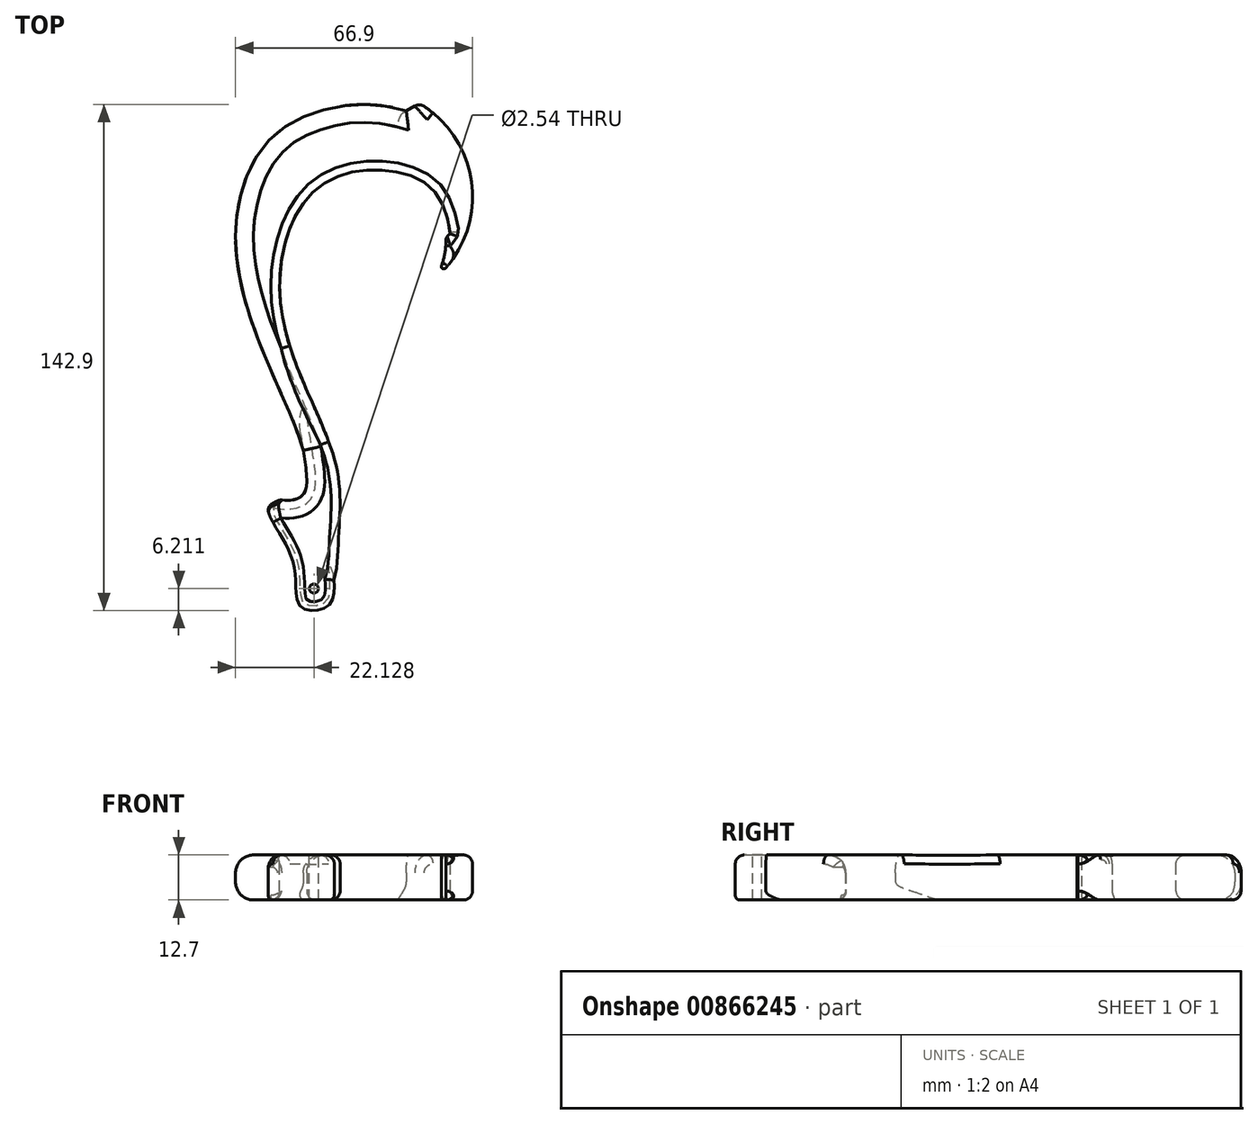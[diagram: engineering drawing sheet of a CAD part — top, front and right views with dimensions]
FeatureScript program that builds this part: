
annotation { "Feature Type Name" : "Feature", "Feature Type Description" : "" }
export const myFeature = defineFeature(function(context is Context, id is Id, definition is map)
    precondition{}
    {
        {
            var Q0;
            Q0=qCreatedBy(makeId("Top.planeOp"),FACE);
            var sketch = newSketch(context, id + "F0", { "sketchPlane" : qUnion([Q0])});
            skFitSpline(sketch, "E0", {"points": [v(12.36, 30.58) * mm, v(0, 47.37) * mm, v(-24.9, 43.6) * mm, v(-35.15, 8.04) * mm, v(-20.04, -34.04) * mm, v(-19.17, -55.17) * mm, v(-20.47, -67.18) * mm], "startDerivative": vector(-26.58, 212.62) * mm, "endDerivative": vector(-34.09, -129.53) * mm});
            skLineSegment(sketch, "E1", {"start": v(12.36, 30.58) * mm, "end": v(11.16, 29.44) * mm});
            skLineSegment(sketch, "E2", {"start": v(3.7, 67.39) * mm, "end": v(0, 65.26) * mm});
            skFitSpline(sketch, "E3", {"points": [v(0, 65.26) * mm, v(-24.38, 65.26) * mm, v(-40.44, 55.04) * mm, v(-48.04, 24.97) * mm, v(-35.77, -13.58) * mm, v(-29.1, -30.6) * mm], "startDerivative": vector(-144.73, 42.7) * mm, "endDerivative": vector(33.48, -115.11) * mm});
            skArc(sketch, "E4", {"start": v(11.16, 20.94) * mm, "mid": v(18.28, 45.9) * mm, "end": v(3.7, 67.39) * mm});
            skArc(sketch, "E5", {"start": v(10.08, 21.93) * mm, "mid": v(10.97, 25.63) * mm, "end": v(11.16, 29.44) * mm});
            skArc(sketch, "E6", {"start": v(10.08, 21.93) * mm, "mid": v(10.1, 20.86) * mm, "end": v(11.16, 20.94) * mm});
            skFitSpline(sketch, "E7", {"points": [v(-29.1, -30.6) * mm, v(-29.1, -42.96) * mm, v(-35.77, -44.53) * mm], "startDerivative": vector(5.3, -33.07) * mm, "endDerivative": vector(-21.74, 3.06) * mm});
            skFitSpline(sketch, "E8", {"points": [v(-35.77, -44.53) * mm, v(-38.98, -47.16) * mm, v(-31.97, -62.05) * mm, v(-29.81, -74.7) * mm, v(-22.03, -74.45) * mm, v(-20.47, -67.18) * mm], "startDerivative": vector(-32.87, -15.99) * mm, "endDerivative": vector(-3.2, 46.84) * mm});
            skSolve(sketch);
        }
        {
            var Q0;
            Q0=makeQuery(id+"F0.imprint","IMPRINT",FACE,{"disambiguationData":[TD([[makeQuery(id+"F0.imprint","IMPRINT",EDGE,{"derivedFrom":sQuery(id+"F0.wireOp",EDGE,"E0")}),-1.0]])]});
            extrude(context, id + "F1", {"entities" : qUnion([Q0]), "depth" : 12.7 * mm, "offsetDistance" : 25.4 * mm});
        }
        {
            var Q0;
            Q0=makeQuery(id+"F1.opExtrude","CAP_EDGE",EDGE,{"disambiguationData":[OSD([sQuery(id+"F0.wireOp",EDGE,"E3")])],"isStart":false});
            var Q1;
            Q1=makeQuery(id+"F1.opExtrude","CAP_EDGE",EDGE,{"disambiguationData":[OSD([sQuery(id+"F0.wireOp",EDGE,"E2")])],"isStart":false});
            var Q2;
            Q2=makeQuery(id+"F1.opExtrude","CAP_EDGE",EDGE,{"disambiguationData":[OSD([sQuery(id+"F0.wireOp",EDGE,"E7")])],"isStart":false});
            fillet(context, id + "F2", {"entities" : qUnion([Q0, Q1, Q2]), "radius" : 5.08 * mm, "tangentPropagation" : true, "allowEdgeOverflow" : false});
        }
        {
            var Q0;
            Q0=makeQuery(id+"F1.opExtrude","CAP_EDGE",EDGE,{"disambiguationData":[OSD([sQuery(id+"F0.wireOp",EDGE,"E0")])],"isStart":false});
            fillet(context, id + "F3", {"entities" : qUnion([Q0]), "radius" : 2.5 * mm, "tangentPropagation" : true, "allowEdgeOverflow" : false});
        }
        {
            var Q0;
            Q0=makeQuery(id+"F1.opExtrude","CAP_EDGE",EDGE,{"disambiguationData":[OSD([sQuery(id+"F0.wireOp",EDGE,"E8")])],"isStart":false});
            var Q1;
            Q1=makeQuery(id+"F1.opExtrude","CAP_EDGE",EDGE,{"disambiguationData":[OSD([sQuery(id+"F0.wireOp",EDGE,"E1")])],"isStart":false});
            fillet(context, id + "F4", {"entities" : qUnion([Q0, Q1]), "radius" : 2.5 * mm, "tangentPropagation" : true, "allowEdgeOverflow" : false});
        }
        {
            var Q0;
            Q0=makeQuery(id+"F1.opExtrude","CAP_EDGE",EDGE,{"disambiguationData":[OSD([sQuery(id+"F0.wireOp",EDGE,"E5")])],"isStart":false});
            fillet(context, id + "F5", {"entities" : qUnion([Q0]), "radius" : 1.27 * mm, "tangentPropagation" : true, "allowEdgeOverflow" : false});
        }
        {
            var Q0;
            Q0=makeQuery(id+"F1.opExtrude","CAP_EDGE",EDGE,{"disambiguationData":[OSD([sQuery(id+"F0.wireOp",EDGE,"E4")])],"isStart":false});
            fillet(context, id + "F6", {"entities" : qUnion([Q0]), "radius" : 2.5 * mm, "tangentPropagation" : true, "allowEdgeOverflow" : false});
        }
        {
            var Q0;
            Q0=makeQuery(id+"F1.opExtrude","CAP_EDGE",EDGE,{"disambiguationData":[OSD([sQuery(id+"F0.wireOp",EDGE,"E3")])],"isStart":true});
            fillet(context, id + "F7", {"entities" : qUnion([Q0]), "radius" : 5.08 * mm, "tangentPropagation" : true, "allowEdgeOverflow" : false});
        }
        {
            var Q0;
            Q0=makeQuery(id+"F1.opExtrude","CAP_EDGE",EDGE,{"disambiguationData":[OSD([sQuery(id+"F0.wireOp",EDGE,"E0")])],"isStart":true});
            fillet(context, id + "F8", {"entities" : qUnion([Q0]), "radius" : 2.5 * mm, "tangentPropagation" : true, "allowEdgeOverflow" : false});
        }
        {
            var Q0;
            Q0=makeQuery(id+"F1.opExtrude","CAP_EDGE",EDGE,{"disambiguationData":[OSD([sQuery(id+"F0.wireOp",EDGE,"E1")])],"isStart":true});
            var Q1;
            {var subQ0=sQuery(id+"F0.wireOp",EDGE,"E5");var subQ1=sQuery(id+"F0.wireOp",EDGE,"E1");Q1=makeQuery(id+"F5.opFillet","BLEND_EDGE",EDGE,{"blendedFrom":[makeQuery(id+"F1.opExtrude","SWEPT_EDGE",EDGE,{"disambiguationData":[OSD([subQ1,subQ0])]}),makeQuery(id+"F1.opExtrude","CAP_FACE",FACE,{"disambiguationData":[OSD([sQuery(id+"F0.wireOp",EDGE,"E0"),subQ1,sQuery(id+"F0.wireOp",EDGE,"E2"),sQuery(id+"F0.wireOp",EDGE,"E3"),sQuery(id+"F0.wireOp",EDGE,"E4"),subQ0,sQuery(id+"F0.wireOp",EDGE,"E6"),sQuery(id+"F0.wireOp",EDGE,"E7"),sQuery(id+"F0.wireOp",EDGE,"E8")])],"isStart":true})],"blendedInto":[makeQuery(id+"F1.opExtrude","CAP_FACE",FACE,{"disambiguationData":[OSD([sQuery(id+"F0.wireOp",EDGE,"E0"),subQ1,sQuery(id+"F0.wireOp",EDGE,"E2"),sQuery(id+"F0.wireOp",EDGE,"E3"),sQuery(id+"F0.wireOp",EDGE,"E4"),subQ0,sQuery(id+"F0.wireOp",EDGE,"E6"),sQuery(id+"F0.wireOp",EDGE,"E7"),sQuery(id+"F0.wireOp",EDGE,"E8")])],"isStart":true})]});}
            fillet(context, id + "F9", {"entities" : qUnion([Q0, Q1]), "radius" : 1.27 * mm, "tangentPropagation" : true, "allowEdgeOverflow" : false});
        }
        {
            var Q0;
            Q0=makeQuery(id+"F1.opExtrude","CAP_EDGE",EDGE,{"disambiguationData":[OSD([sQuery(id+"F0.wireOp",EDGE,"E4")])],"isStart":true});
            fillet(context, id + "F10", {"entities" : qUnion([Q0]), "radius" : 2.5 * mm, "tangentPropagation" : true, "allowEdgeOverflow" : false});
        }
        {
            var Q0;
            Q0=makeQuery(id+"F1.opExtrude","CAP_EDGE",EDGE,{"disambiguationData":[OSD([sQuery(id+"F0.wireOp",EDGE,"E8")])],"isStart":true});
            fillet(context, id + "F11", {"entities" : qUnion([Q0]), "radius" : 2.5 * mm, "tangentPropagation" : true, "allowEdgeOverflow" : false});
        }
        {
            var Q0;
            Q0=makeQuery(id+"F1.opExtrude","CAP_EDGE",EDGE,{"disambiguationData":[OSD([sQuery(id+"F0.wireOp",EDGE,"E8")])],"isStart":true});
            fillet(context, id + "F12", {"entities" : qUnion([Q0]), "radius" : 1.27 * mm, "tangentPropagation" : true, "allowEdgeOverflow" : false});
        }
        {
            var Q0;
            Q0=makeQuery(id+"F3.opFillet","SPLIT",FACE,{"disambiguationData":[OD(1.0)],"derivedFrom":makeQuery(id+"F1.opExtrude","CAP_FACE",FACE,{"disambiguationData":[OSD([sQuery(id+"F0.wireOp",EDGE,"E0"),sQuery(id+"F0.wireOp",EDGE,"E1"),sQuery(id+"F0.wireOp",EDGE,"E2"),sQuery(id+"F0.wireOp",EDGE,"E3"),sQuery(id+"F0.wireOp",EDGE,"E4"),sQuery(id+"F0.wireOp",EDGE,"E5"),sQuery(id+"F0.wireOp",EDGE,"E6"),sQuery(id+"F0.wireOp",EDGE,"E7"),sQuery(id+"F0.wireOp",EDGE,"E8")])],"isStart":false})});
            var sketch = newSketch(context, id + "F13", { "sketchPlane" : qUnion([Q0])});
            skPoint(sketch, "E9", {"position": v(-26.1, -69.6) * mm});
            skSolve(sketch);
        }
        {
            var Q0;
            Q0=sQuery(id+"F13.wireOp",VERTEX,"E9");
            var Q1;
            Q1=makeQuery(id+"F1.opExtrude","SWEPT_BODY",BODY,{"disambiguationData":[OSD([sQuery(id+"F0.wireOp",EDGE,"E0"),sQuery(id+"F0.wireOp",EDGE,"E1"),sQuery(id+"F0.wireOp",EDGE,"E2"),sQuery(id+"F0.wireOp",EDGE,"E3"),sQuery(id+"F0.wireOp",EDGE,"E4"),sQuery(id+"F0.wireOp",EDGE,"E5"),sQuery(id+"F0.wireOp",EDGE,"E6"),sQuery(id+"F0.wireOp",EDGE,"E7"),sQuery(id+"F0.wireOp",EDGE,"E8")])]});
            hole(context, id + "F14", {"style" : HoleStyle.SIMPLE, "endStyle" : HoleEndStyle.THROUGH, "holeDiameter" : 2.54 * mm, "majorDiameter" : 6.35 * mm, "isTappedThrough" : true, "tappedDepth" : 12.7 * mm, "tapClearance" : 3, "locations" : qUnion([Q0]), "scope" : qUnion([Q1])});
        }
    });
